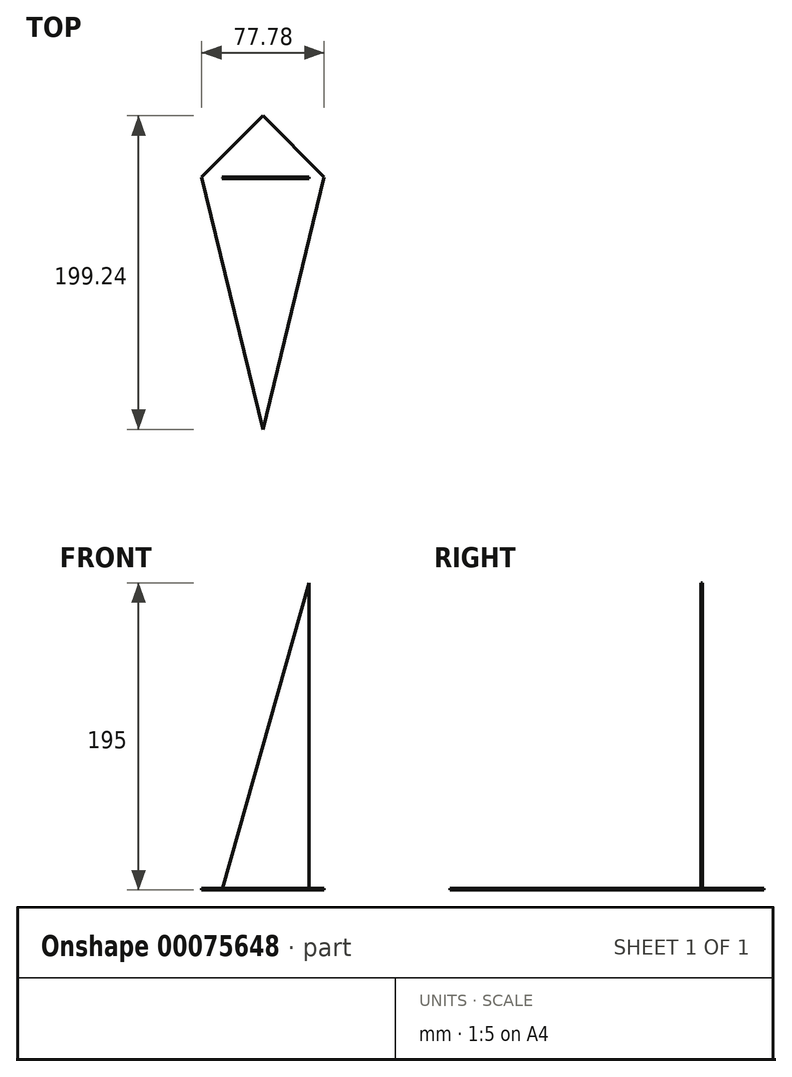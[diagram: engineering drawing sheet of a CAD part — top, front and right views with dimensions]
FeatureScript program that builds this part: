
annotation { "Feature Type Name" : "Feature", "Feature Type Description" : "" }
export const myFeature = defineFeature(function(context is Context, id is Id, definition is map)
    precondition{}
    {
        {
            var Q0;
            Q0=qCreatedBy(makeId("Top.planeOp"),FACE);
            var sketch = newSketch(context, id + "F0", { "sketchPlane" : qUnion([Q0])});
            skLineSegment(sketch, "E0", {"start": v(-38.9, 0) * mm, "end": v(0, -160.35) * mm});
            skLineSegment(sketch, "E1", {"start": v(0, -160.35) * mm, "end": v(38.9, 0) * mm});
            skLineSegment(sketch, "E2", {"start": v(-38.9, 0) * mm, "end": v(0, 38.9) * mm});
            skLineSegment(sketch, "E3", {"start": v(0, 38.9) * mm, "end": v(38.9, 0) * mm});
            skLineSegment(sketch, "E4", {"start": v(-38.9, 0) * mm, "end": v(38.9, 0) * mm});
            skSolve(sketch);
        }
        {
            var Q0;
            Q0=makeQuery(id+"F0.imprint","IMPRINT",FACE,{"disambiguationData":[TD([[makeQuery(id+"F0.imprint","IMPRINT",EDGE,{"derivedFrom":sQuery(id+"F0.wireOp",EDGE,"E2")}),-1.0]])]});
            var Q1;
            Q1=makeQuery(id+"F0.imprint","IMPRINT",FACE,{"disambiguationData":[TD([[makeQuery(id+"F0.imprint","IMPRINT",EDGE,{"derivedFrom":sQuery(id+"F0.wireOp",EDGE,"E0")}),1.0]])]});
            extrude(context, id + "F1", {"entities" : qUnion([Q0, Q1]), "depth" : 1 * mm});
        }
        {
            var Q0;
            Q0=qCreatedBy(makeId("Front.planeOp"),FACE);
            var sketch = newSketch(context, id + "F2", { "sketchPlane" : qUnion([Q0])});
            skLineSegment(sketch, "E5", {"start": v(-25.84, 0) * mm, "end": v(29.16, 0) * mm});
            skLineSegment(sketch, "E6", {"start": v(29.16, 0) * mm, "end": v(29.16, 195) * mm});
            skLineSegment(sketch, "E7", {"start": v(29.16, 195) * mm, "end": v(-25.84, 0) * mm});
            skSolve(sketch);
        }
        {
            var Q0;
            Q0 = qSketchRegion(id + "F2", true);
            var Q1;
            Q1=makeQuery(id+"F2.imprint","IMPRINT",FACE,{"disambiguationData":[TD([[makeQuery(id+"F2.imprint","IMPRINT",EDGE,{"derivedFrom":sQuery(id+"F2.wireOp",EDGE,"E5")}),1.0]])]});
            extrude(context, id + "F3", {"entities" : qUnion([Q0, Q1]), "depth" : 1 * mm});
        }
    });
